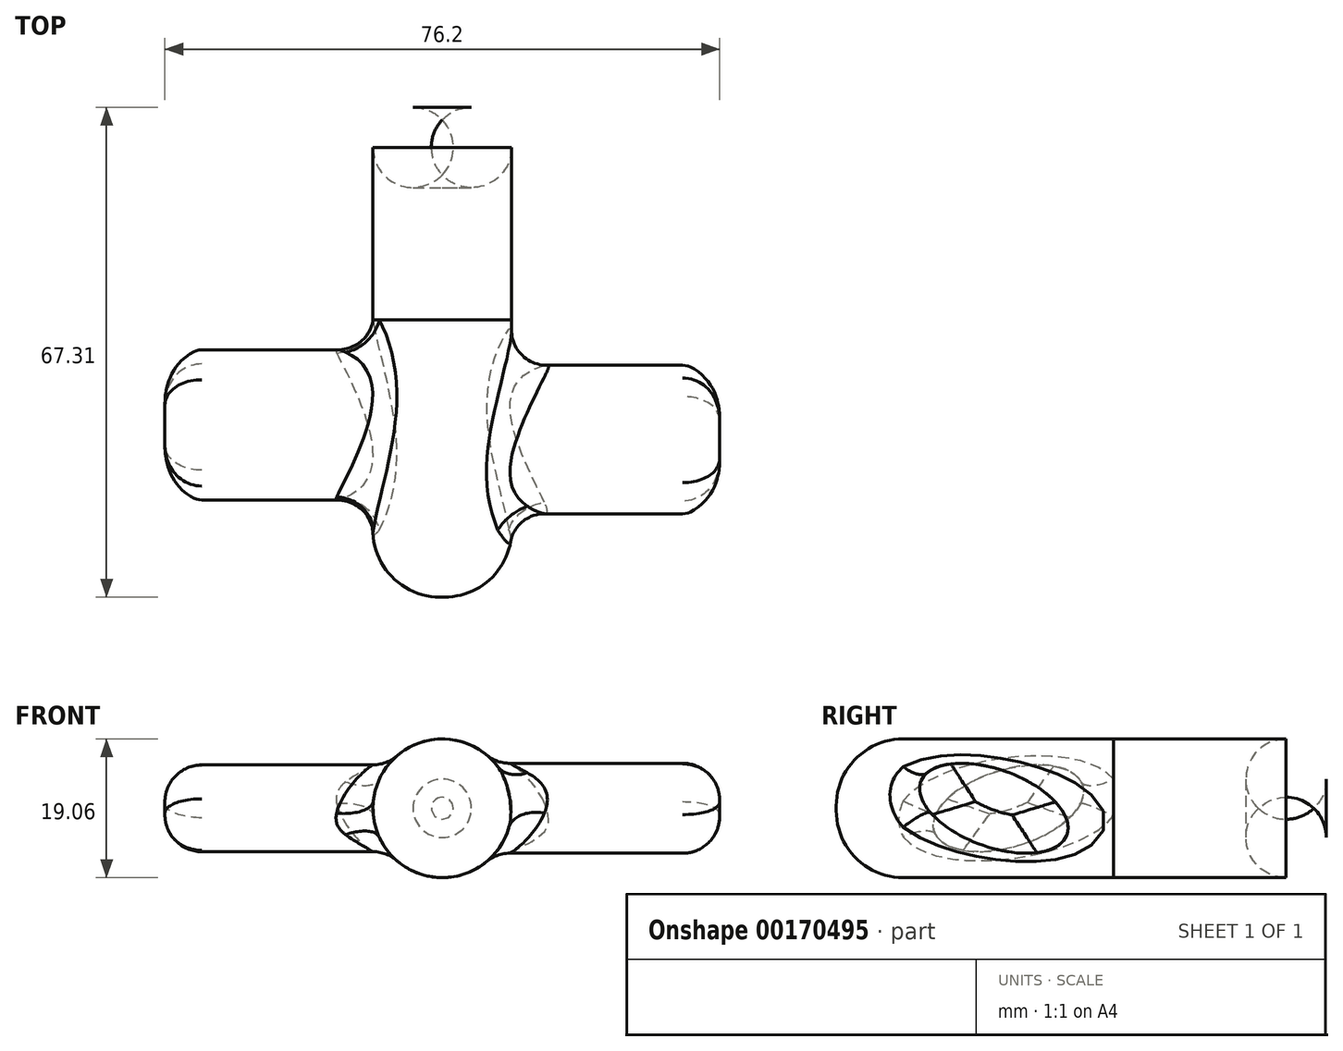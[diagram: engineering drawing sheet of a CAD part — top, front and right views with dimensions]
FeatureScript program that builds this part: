
annotation { "Feature Type Name" : "Feature", "Feature Type Description" : "" }
export const myFeature = defineFeature(function(context is Context, id is Id, definition is map)
    precondition{}
    {
        {
            var Q0;
            Q0=qCreatedBy(makeId("Front.planeOp"),FACE);
            var sketch = newSketch(context, id + "F0", { "sketchPlane" : qUnion([Q0])});
            skCircle(sketch, "E0", {"center": v(0, 0) * mm, "radius": 9.53 * mm});
            skSolve(sketch);
        }
        {
            var Q0;
            Q0=makeQuery(id+"F0.imprint","IMPRINT",FACE,{"disambiguationData":[TD([[makeQuery(id+"F0.imprint","IMPRINT",EDGE,{"derivedFrom":sQuery(id+"F0.wireOp",EDGE,"E0")}),1.0]])]});
            extrude(context, id + "F1", {"entities" : qUnion([Q0]), "oppositeDirection" : true, "depth" : 29.2 * mm});
        }
        {
            var Q0;
            Q0=makeQuery(id+"F1.opExtrude","CAP_EDGE",EDGE,{"disambiguationData":[OSD([sQuery(id+"F0.wireOp",EDGE,"E0")])],"isStart":false});
            fillet(context, id + "F2", {"entities" : qUnion([Q0]), "radius" : 5.52 * mm, "tangentPropagation" : true, "allowEdgeOverflow" : false});
        }
        {
            var Q0;
            Q0=makeQuery(id+"F1.opExtrude","CAP_FACE",FACE,{"disambiguationData":[OSD([sQuery(id+"F0.wireOp",EDGE,"E0")])],"isStart":true});
            extrude(context, id + "F3", {"entities" : qUnion([Q0]), "depth" : 38.1 * mm});
        }
        {
            var Q0;
            Q0=makeQuery(id+"F3.opExtrude","CAP_EDGE",EDGE,{"disambiguationData":[OSD([sQuery(id+"F0.wireOp",EDGE,"E0")])],"isStart":false});
            fillet(context, id + "F4", {"entities" : qUnion([Q0]), "radius" : 9.2 * mm, "tangentPropagation" : true, "allowEdgeOverflow" : false});
        }
        {
            var Q0;
            Q0=qCreatedBy(makeId("Right.planeOp"),FACE);
            var sketch = newSketch(context, id + "F5", { "sketchPlane" : qUnion([Q0])});
            skEllipse(sketch, "E1", {"center": v(-16.45, 0) * mm, "majorRadius": 10.68 * mm, "minorRadius": 5.3 * mm, "majorAxis": v(0.94, -0.34)});
            skSolve(sketch);
        }
        {
            var Q0;
            Q0 = qSketchRegion(id + "F5", true);
            extrude(context, id + "F6", {"entities" : qUnion([Q0]), "operationType" : NewBodyOperationType.ADD, "depth" : 38.1 * mm});
        }
        {
            var Q0;
            Q0=makeQuery(id+"F6.opExtrude","SWEPT_FACE",FACE,{"disambiguationData":[OSD([sQuery(id+"F5.wireOp",EDGE,"E1")])]});
            fillet(context, id + "F7", {"entities" : qUnion([Q0]), "radius" : 5.08 * mm, "tangentPropagation" : true, "allowEdgeOverflow" : false});
        }
        {
            var Q0;
            Q0=qCreatedBy(makeId("Right.planeOp"),FACE);
            var sketch = newSketch(context, id + "F8", { "sketchPlane" : qUnion([Q0])});
            skEllipse(sketch, "E2", {"center": v(-14.44, 0) * mm, "majorRadius": 10.68 * mm, "minorRadius": 5.3 * mm, "majorAxis": v(0.96, 0.3)});
            skSolve(sketch);
        }
        {
            var Q0;
            Q0 = qSketchRegion(id + "F8", true);
            extrude(context, id + "F9", {"entities" : qUnion([Q0]), "operationType" : NewBodyOperationType.ADD, "oppositeDirection" : true, "depth" : 38.1 * mm});
        }
        {
            var Q0;
            Q0=makeQuery(id+"F9.opExtrude","SWEPT_FACE",FACE,{"disambiguationData":[OSD([sQuery(id+"F8.wireOp",EDGE,"E2")])]});
            fillet(context, id + "F10", {"entities" : qUnion([Q0]), "radius" : 5.08 * mm, "tangentPropagation" : true, "allowEdgeOverflow" : false});
        }
    });
